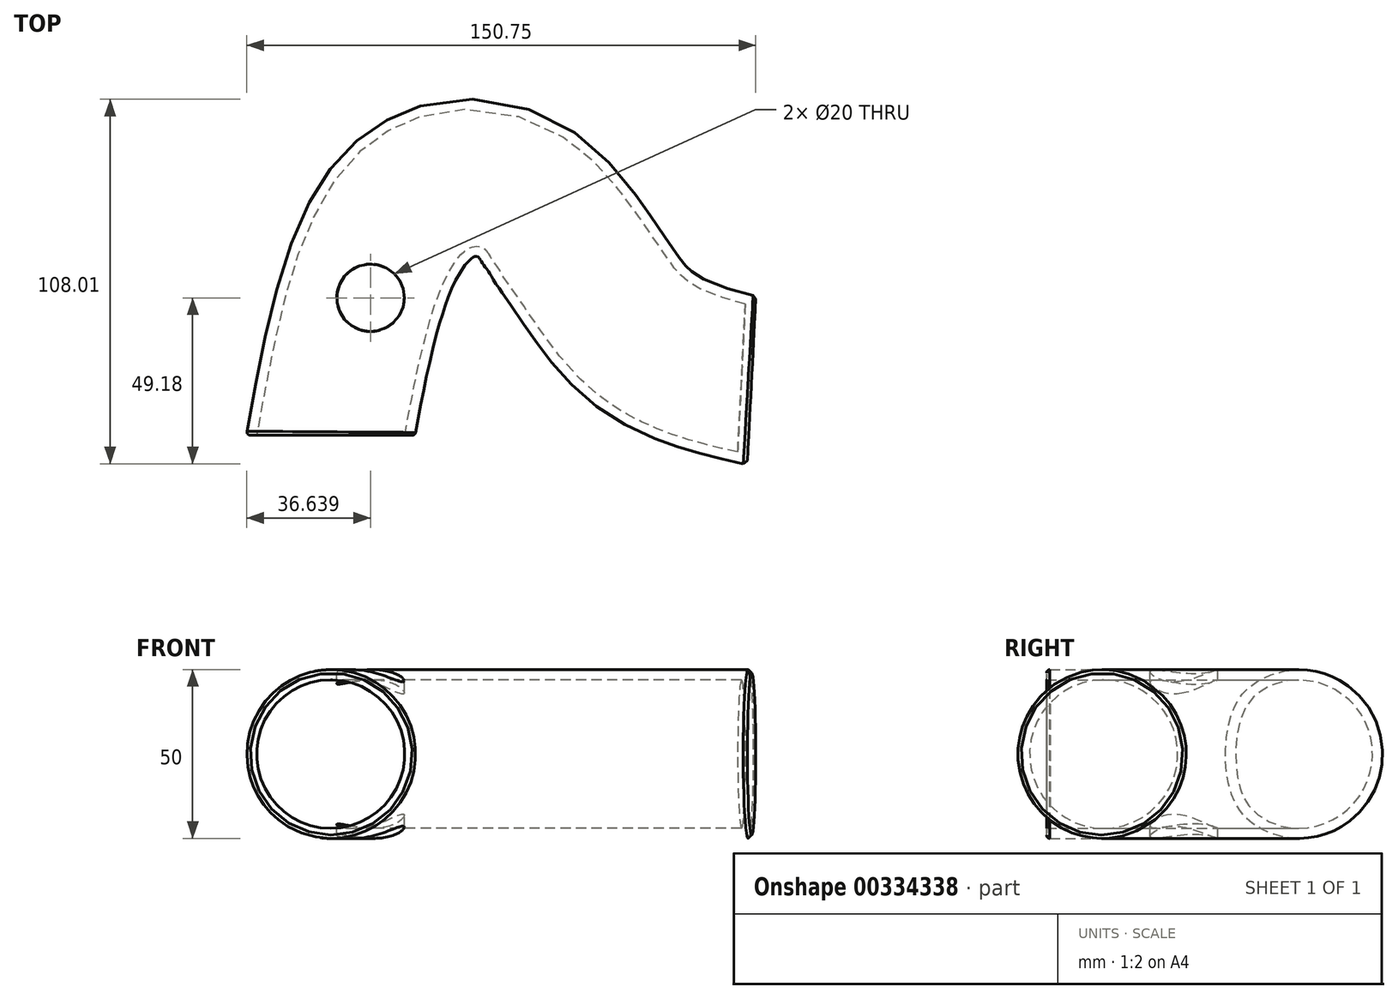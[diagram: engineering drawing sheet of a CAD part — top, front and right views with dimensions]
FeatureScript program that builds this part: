
annotation { "Feature Type Name" : "Feature", "Feature Type Description" : "" }
export const myFeature = defineFeature(function(context is Context, id is Id, definition is map)
    precondition{}
    {
        {
            var Q0;
            Q0=qCreatedBy(makeId("Front.planeOp"),FACE);
            var sketch = newSketch(context, id + "F0", { "sketchPlane" : qUnion([Q0])});
            skCircle(sketch, "E0", {"center": v(0, 0) * mm, "radius": 25 * mm});
            skSolve(sketch);
        }
        {
            var Q0;
            Q0=qCreatedBy(makeId("Top.planeOp"),FACE);
            var sketch = newSketch(context, id + "F1", { "sketchPlane" : qUnion([Q0])});
            skFitSpline(sketch, "E1", {"points": [v(0, 0) * mm, v(24.82, 69.23) * mm, v(58.22, 69.23) * mm, v(89.95, 31.35) * mm, v(124.66, 16.24) * mm], "startDerivative": vector(51.44, 279.14) * mm, "endDerivative": vector(166.9, -39.7) * mm});
            skSolve(sketch);
        }
        {
            var Q0;
            Q0=makeQuery(id+"F0.imprint","IMPRINT",FACE,{"disambiguationData":[TD([[makeQuery(id+"F0.imprint","IMPRINT",EDGE,{"derivedFrom":sQuery(id+"F0.wireOp",EDGE,"E0")}),1.0]])]});
            var Q1;
            Q1=sQuery(id+"F0.wireOp",EDGE,"E0");
            var Q2;
            Q2=sQuery(id+"F1.wireOp",EDGE,"E1");
            sweep(context, id + "F2", {"profiles" : qUnion([Q0]), "surfaceProfiles" : qUnion([Q1]), "path" : qUnion([Q2])});
        }
        {
            var Q0;
            Q0=makeQuery(id+"F2.opSweep","CAP_FACE",FACE,{"disambiguationData":[OSD([sQuery(id+"F0.wireOp",EDGE,"E0"),sQuery(id+"F1.wireOp",VERTEX,"E1.start")])],"isStart":true});
            shell(context, id + "F3", {"entities" : qUnion([Q0]), "thickness" : 3 * mm});
        }
        {
            var Q0;
            Q0=qCreatedBy(makeId("Top.planeOp"),FACE);
            cPlane(context, id + "F4", {"entities" : qUnion([Q0]), "cplaneType" : CPlaneType.OFFSET, "offset" : 25 * mm, "width" : 150 * mm, "height" : 150 * mm});
        }
        {
            var Q0;
            Q0=qCreatedBy(id+"F4.planeOp",FACE);
            var sketch = newSketch(context, id + "F5", { "sketchPlane" : qUnion([Q0])});
            skCircle(sketch, "E2", {"center": v(11.79, 40.72) * mm, "radius": 10 * mm});
            skSolve(sketch);
        }
        {
            var Q0;
            Q0=sQuery(id+"F5.wireOp",VERTEX,"E2.center");
            var Q1;
            Q1=makeQuery(id+"F2.opSweep","SWEPT_BODY",BODY,{"disambiguationData":[OSD([sQuery(id+"F0.wireOp",EDGE,"E0"),sQuery(id+"F1.wireOp",EDGE,"E1")])]});
            hole(context, id + "F6", {"style" : HoleStyle.SIMPLE, "endStyle" : HoleEndStyle.THROUGH, "holeDiameter" : 20 * mm, "tappedDepth" : 12 * mm, "tapClearance" : 3, "locations" : qUnion([Q0]), "scope" : qUnion([Q1])});
        }
        {
            var Q0;
            Q0=makeQuery(id+"F2.opSweep","CAP_EDGE",EDGE,{"disambiguationData":[OSD([sQuery(id+"F0.wireOp",EDGE,"E0"),sQuery(id+"F1.wireOp",VERTEX,"E1.start")])],"isStart":true});
            fillet(context, id + "F7", {"entities" : qUnion([Q0]), "radius" : 1 * mm, "tangentPropagation" : true, "allowEdgeOverflow" : false});
        }
        {
            var Q0;
            Q0=makeQuery(id+"F2.opSweep","CAP_EDGE",EDGE,{"disambiguationData":[OSD([sQuery(id+"F0.wireOp",EDGE,"E0"),sQuery(id+"F1.wireOp",VERTEX,"E1.end")])],"isStart":false});
            chamfer(context, id + "F8", {"entities" : qUnion([Q0]), "width" : 1 * mm, "tangentPropagation" : true});
        }
        {
            var Q0;
            Q0=makeQuery(id+"F2.opSweep","CAP_FACE",FACE,{"disambiguationData":[OSD([sQuery(id+"F0.wireOp",EDGE,"E0"),sQuery(id+"F1.wireOp",VERTEX,"E1.end")])],"isStart":false});
            cPlane(context, id + "F9", {"entities" : qUnion([Q0]), "cplaneType" : CPlaneType.OFFSET, "offset" : 0 * mm, "width" : 150 * mm, "height" : 150 * mm});
        }
    });
